# Revit family: QF_BPRO_RWR 161_572936
name_source: partatom
category: Sonderausstattung
revit_build: Autodesk Revit 2018 (Build: 20190510_1515(x64)
units: mm (PartAtom-declared; Revit-internal decimal feet)

## family parameters
Arbeitsebenenbasiert = Nein
Beim Laden mit Abzugskörper schneiden = Nein
Bemaßung runder Anschluss = Durchmesser verwenden
Gemeinsam genutzt = Nein
Immer vertikal = Ja
Raumberechnungspunkt = Ja
Teiletyp = Normal

## types (1)
- RWR 161
    Abstand Einlagen = 73 mm
    Anzahl Schienen = 18
    Artikel Nummer = 572936
    Beschreibung = Regalwagen aus rostfreiem Edelstahl
Auflagenabstand: 18 Paar 73 mm
Kapazität: 18 GN 2/1 oder  36 GN 1/1
Tragfähigkeit: 200 kg
Wandabweiser aus Kunststoff (Polyamid) an allen vier Ecken
    Beschreibung durch Hersteller analog Leistungsverzeichniskurztext = Abmessungen

Länge:			  662 mm
Breite:			  733 mm
Höhe:			1645 mm

Lichtes Maß:
Abstand der Auflagenschienen:	    73 mm


Ausführung

Der Regalwagen besteht aus CNS 18/10, Werkstoff-Nr. 1.4301. Zwischen stabilem Vierkant-rohr mit 25 x 25 mm (gebogen ohne Einzug) befinden sich eingeschweißte U-Profil-Führungsschienen. Diese sind mit einer Kippsicherung sowie einer beidseitigen Durchschubsicherung für GN 2/1, 1/1, und 2/4 versehen.
Ein eingeschweißtes Vierkantrohr 20 x 10 mm auf mittlerer Höhe des Regalwagens, jeweils an Vorder- und Rückseite höhenversetzt angebracht, verstärkt zusätzlich die Stabilität.

Der Regalwagen ist fahrbar mittels rostfreien Kunststoffrollen gemäß DIN 18867, Teil 8
(4 Lenkrollen, davon 2 mit Feststeller, Rollendurchmesser 125 mm). Wandabweiser aus Kunststoff (Polyamid) an allen vier Ecken schützen vor Beschädigung.

Zubehör/ Optionen

•	Staubschutzhaube aus durchsichtigem PE (Best.Nr. 568 772)
•	Isolierhaube aus PE, beidseitig aluminiert (Best.Nr. 568 775)
•	Wagendach aus CNS
•	CNS-Verkleidung, 2- oder 3-seitig
•	Transportsicherungsbügel, beidseitig
•	Schiebegriff stirnseitig


 
Technische Daten

Werkstoff:		Chromnickelstahl 18/10,
		                        Polyamid (PA)
Materialstärke VK-Rohr:	1,5 mm
Materialstärke
Auflageschienen:		1,2 mm
Gewicht:		                        23,1 kg
Tragfähigkeit je Wagen:	200 kg
Anzahl Auflagenpaare:	18
Kapazität:	18 x GN 2/1 oder
		36 x GN 1/1


Besonderheit

•	U-Profil-Führungsschienen mit Kipp- und beidseitiger Durchschubsicherung


Fabrikat

Hersteller:	B.PRO
Typ:                                       RWR 161
Best.Nr.		572 936
    Beschreibung durch Hersteller analog Leistungsverzeichnislangtext = Abmessungen

Länge:			  662 mm
Breite:			  733 mm
Höhe:			1645 mm

Lichtes Maß:
Abstand der Auflagenschienen:	    73 mm


Ausführung

Der Regalwagen besteht aus CNS 18/10, Werkstoff-Nr. 1.4301. Zwischen stabilem Vierkant-rohr mit 25 x 25 mm (gebogen ohne Einzug) befinden sich eingeschweißte U-Profil-Führungsschienen. Diese sind mit einer Kippsicherung sowie einer beidseitigen Durchschubsicherung für GN 2/1, 1/1, und 2/4 versehen.
Ein eingeschweißtes Vierkantrohr 20 x 10 mm auf mittlerer Höhe des Regalwagens, jeweils an Vorder- und Rückseite höhenversetzt angebracht, verstärkt zusätzlich die Stabilität.

Der Regalwagen ist fahrbar mittels rostfreien Kunststoffrollen gemäß DIN 18867, Teil 8
(4 Lenkrollen, davon 2 mit Feststeller, Rollendurchmesser 125 mm). Wandabweiser aus Kunststoff (Polyamid) an allen vier Ecken schützen vor Beschädigung.

Zubehör/ Optionen

•	Staubschutzhaube aus durchsichtigem PE (Best.Nr. 568 772)
•	Isolierhaube aus PE, beidseitig aluminiert (Best.Nr. 568 775)
•	Wagendach aus CNS
•	CNS-Verkleidung, 2- oder 3-seitig
•	Transportsicherungsbügel, beidseitig
•	Schiebegriff stirnseitig


 
Technische Daten

Werkstoff:		Chromnickelstahl 18/10,
		                        Polyamid (PA)
Materialstärke VK-Rohr:	1,5 mm
Materialstärke
Auflageschienen:		1,2 mm
Gewicht:		                        23,1 kg
Tragfähigkeit je Wagen:	200 kg
Anzahl Auflagenpaare:	18
Kapazität:	18 x GN 2/1 oder
		36 x GN 1/1


Besonderheit

•	U-Profil-Führungsschienen mit Kipp- und beidseitiger Durchschubsicherung


Fabrikat

Hersteller:	B.PRO
Typ:                                       RWR 161
Best.Nr.		572 936
    Gerätegewicht Netto = 23.10 kg
    Großküchengerätezuordnung = Ja
    Hersteller = B.PRO GmbH
    Höhe = 1645 mm
    Internetadresse Gerätehersteller = https://www.bpro-solutions.com
    Internetadresse für Ersatzteilliste = https://www.bpro-solutions.com
    Kosten = 590.2 $
    Länge Gerätebreite = 662 mm  [stored 2.17192 ft]
    Länge Korpus = 587 mm  [stored 1.92585 ft]
    Material = QF_Metal-Stainless-Steel_general
    Material_Stoßschutz = QF_Rubber-Black-Matt
    Modell = RWR 161
    Sockelhöhe = 174 mm  [stored 0.570866 ft]
    Tiefe = 733 mm  [stored 2.40486 ft]
    Tiefe Korpus = 658 mm  [stored 2.15879 ft]
    Typenkommentare = Regalwagen, 1-teilig
    URL = https://www.bpro-solutions.com
    Versatz Einlage unten = 65 mm
    Zubehör = Nein

note: [stored X ft] marks values corroborated as IEEE doubles in the binary element streams (Revit-internal decimal feet)
